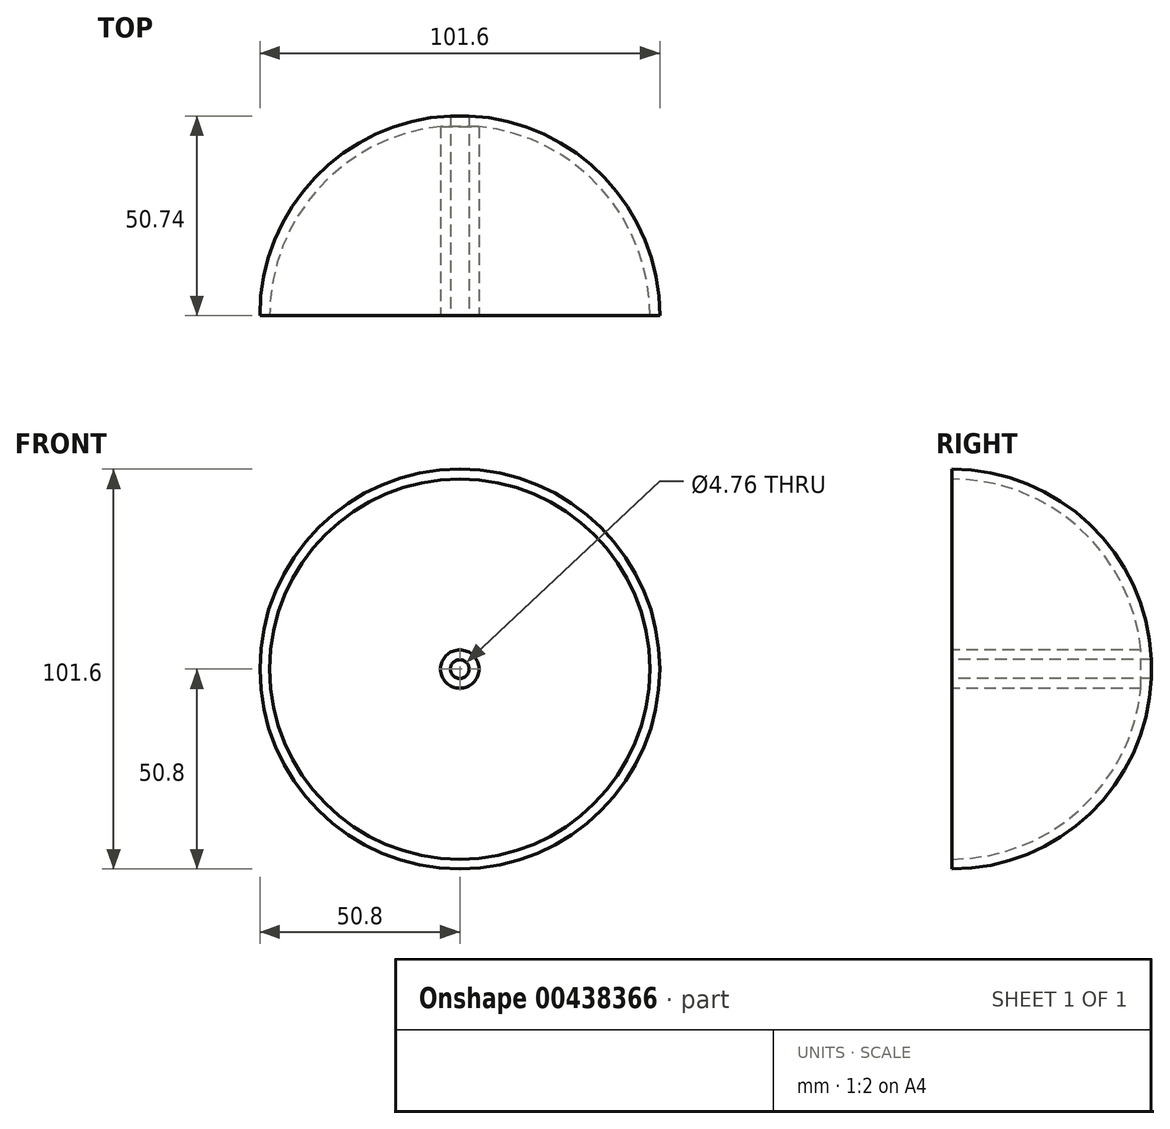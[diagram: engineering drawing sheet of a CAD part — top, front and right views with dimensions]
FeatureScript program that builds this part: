
annotation { "Feature Type Name" : "Feature", "Feature Type Description" : "" }
export const myFeature = defineFeature(function(context is Context, id is Id, definition is map)
    precondition{}
    {
        {
            var Q0;
            Q0=qCreatedBy(makeId("Front.planeOp"),FACE);
            var sketch = newSketch(context, id + "F0", { "sketchPlane" : qUnion([Q0])});
            skCircle(sketch, "E0", {"center": v(0, 0) * mm, "radius": 50.8 * mm});
            skLineSegment(sketch, "E1", {"start": v(0, 0) * mm, "end": v(0, -50.8) * mm});
            skLineSegment(sketch, "E2", {"start": v(0, 0) * mm, "end": v(0, 50.8) * mm});
            skSolve(sketch);
        }
        {
            var Q0;
            {var subQ0=sQuery(id+"F0.wireOp",EDGE,"E1");var subQ1=sQuery(id+"F0.wireOp",EDGE,"E0");var subQ2=makeQuery(id+"F0.imprint","INTERSECT",VERTEX,{"derivedFrom":[subQ1,subQ0]});Q0=makeQuery(id+"F0.imprint","IMPRINT",FACE,{"disambiguationData":[TD([[makeQuery(id+"F0.imprint","IMPRINT",EDGE,{"disambiguationData":[TD([[subQ2,-1.0]])],"derivedFrom":subQ1}),1.0]])]});}
            var Q1;
            Q1=sQuery(id+"F0.wireOp",EDGE,"E2");
            revolve(context, id + "F1", {"entities" : qUnion([Q0]), "axis" : qUnion([Q1]), "revolveType" : RevolveType.ONE_DIRECTION, "angle" : 180 * degree});
        }
        {
            var Q0;
            Q0=sQuery(id+"F0.wireOp",VERTEX,"E1.start");
            var Q1;
            Q1=makeQuery(id+"F1.opRevolve","SWEPT_BODY",BODY,{"disambiguationData":[OSD([sQuery(id+"F0.wireOp",EDGE,"E0"),sQuery(id+"F0.wireOp",EDGE,"E1"),sQuery(id+"F0.wireOp",EDGE,"E2"),sQuery(id+"F0.wireOp",EDGE,"ZdVR4FbW-Q4KG-WWf3-acfr-Kf22NxFX0rOm")])]});
            hole(context, id + "F2", {"style" : HoleStyle.SIMPLE, "endStyle" : HoleEndStyle.THROUGH, "holeDiameter" : 4.76 * mm, "isTappedThrough" : true, "tappedDepth" : 12.7 * mm, "tapClearance" : 3, "locations" : qUnion([Q0]), "scope" : qUnion([Q1])});
        }
        {
            var Q0;
            Q0=sQuery(id+"F0.wireOp",VERTEX,"E1.start");
            var Q1;
            Q1=makeQuery(id+"F1.opRevolve","SWEPT_BODY",BODY,{"disambiguationData":[OSD([sQuery(id+"F0.wireOp",EDGE,"E0"),sQuery(id+"F0.wireOp",EDGE,"E1"),sQuery(id+"F0.wireOp",EDGE,"E2"),sQuery(id+"F0.wireOp",EDGE,"ZdVR4FbW-Q4KG-WWf3-acfr-Kf22NxFX0rOm")])]});
            hole(context, id + "F3", {"style" : HoleStyle.SIMPLE, "endStyle" : HoleEndStyle.THROUGH, "oppositeDirection" : true, "holeDiameter" : 4.76 * mm, "isTappedThrough" : true, "tappedDepth" : 12.7 * mm, "tapClearance" : 3, "locations" : qUnion([Q0]), "scope" : qUnion([Q1])});
        }
        {
            var Q0;
            Q0=makeQuery(id+"F1.opRevolve","CAP_FACE",FACE,{"disambiguationData":[OSD([sQuery(id+"F0.wireOp",EDGE,"E0"),sQuery(id+"F0.wireOp",EDGE,"E1"),sQuery(id+"F0.wireOp",EDGE,"E2")])],"isStart":true});
            shell(context, id + "F4", {"entities" : qUnion([Q0]), "thickness" : 2.5 * mm});
        }
    });
